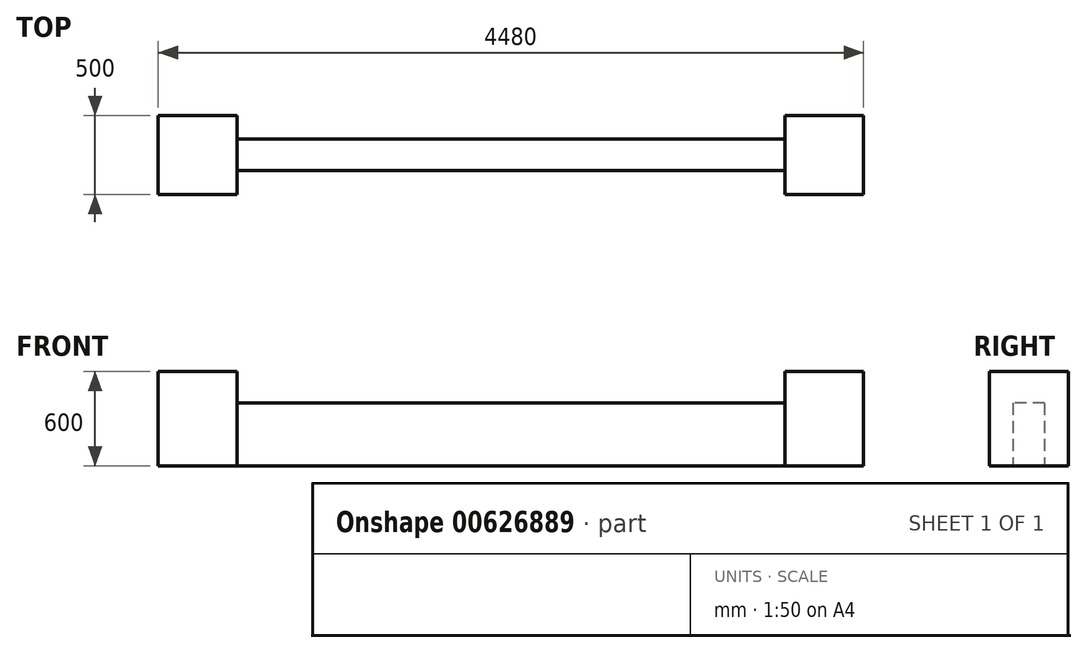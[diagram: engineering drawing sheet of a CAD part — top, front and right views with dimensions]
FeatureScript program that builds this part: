
annotation { "Feature Type Name" : "Feature", "Feature Type Description" : "" }
export const myFeature = defineFeature(function(context is Context, id is Id, definition is map)
    precondition{}
    {
        {
            var Q0;
            Q0=qCreatedBy(makeId("Top.planeOp"),FACE);
            var sketch = newSketch(context, id + "F0", { "sketchPlane" : qUnion([Q0])});
            skLineSegment(sketch, "E0", {"start": v(-1541.48, -106.4) * mm, "end": v(-1541.48, -606.4) * mm});
            skLineSegment(sketch, "E1", {"start": v(-1541.48, -606.4) * mm, "end": v(-1041.48, -606.4) * mm});
            skLineSegment(sketch, "E2", {"start": v(-1041.48, -606.4) * mm, "end": v(-1041.48, -456.4) * mm});
            skLineSegment(sketch, "E3", {"start": v(-1041.48, -456.4) * mm, "end": v(2438.52, -456.4) * mm});
            skLineSegment(sketch, "E4", {"start": v(2438.52, -456.4) * mm, "end": v(2438.52, -606.4) * mm});
            skLineSegment(sketch, "E5", {"start": v(2438.52, -606.4) * mm, "end": v(2938.52, -606.4) * mm});
            skLineSegment(sketch, "E6", {"start": v(2938.52, -606.4) * mm, "end": v(2938.52, -106.4) * mm});
            skLineSegment(sketch, "E7", {"start": v(2938.52, -106.4) * mm, "end": v(2438.52, -106.4) * mm});
            skLineSegment(sketch, "E8", {"start": v(2438.52, -106.4) * mm, "end": v(2438.52, -256.4) * mm});
            skLineSegment(sketch, "E9", {"start": v(2438.52, -256.4) * mm, "end": v(-1041.48, -256.4) * mm});
            skLineSegment(sketch, "E10", {"start": v(-1041.48, -256.4) * mm, "end": v(-1041.48, -106.4) * mm});
            skLineSegment(sketch, "E11", {"start": v(-1541.48, -106.4) * mm, "end": v(-1041.48, -106.4) * mm});
            skLineSegment(sketch, "E12", {"start": v(-1081.48, 332.04) * mm, "end": v(-1081.48, -1348.1) * mm, "construction": true});
            skLineSegment(sketch, "E13", {"start": v(2478.52, 358.87) * mm, "end": v(2478.52, -1348.1) * mm, "construction": true});
            skLineSegment(sketch, "E14", {"start": v(698.52, 382.34) * mm, "end": v(698.52, -1673.4) * mm, "construction": true});
            skSolve(sketch);
        }
        {
            var Q0;
            Q0 = qSketchRegion(id + "F0", true);
            extrude(context, id + "F1", {"entities" : qUnion([Q0]), "depth" : 400 * mm, "offsetDistance" : 25 * mm});
        }
        {
            var Q0;
            Q0=makeQuery(id+"F1.opExtrude","CAP_FACE",FACE,{"disambiguationData":[OSD([sQuery(id+"F0.wireOp",EDGE,"E0"),sQuery(id+"F0.wireOp",EDGE,"E1"),sQuery(id+"F0.wireOp",EDGE,"E2"),sQuery(id+"F0.wireOp",EDGE,"E3"),sQuery(id+"F0.wireOp",EDGE,"E4"),sQuery(id+"F0.wireOp",EDGE,"E5"),sQuery(id+"F0.wireOp",EDGE,"E6"),sQuery(id+"F0.wireOp",EDGE,"E7"),sQuery(id+"F0.wireOp",EDGE,"E8"),sQuery(id+"F0.wireOp",EDGE,"E9"),sQuery(id+"F0.wireOp",EDGE,"E10"),sQuery(id+"F0.wireOp",EDGE,"E11")])],"isStart":false});
            var sketch = newSketch(context, id + "F2", { "sketchPlane" : qUnion([Q0])});
            skLineSegment(sketch, "E15.bottom", {"start": v(-1541.48, -106.4) * mm, "end": v(-1041.48, -106.4) * mm});
            skLineSegment(sketch, "E15.top", {"start": v(-1541.48, -606.4) * mm, "end": v(-1041.48, -606.4) * mm});
            skLineSegment(sketch, "E15.left", {"start": v(-1541.48, -106.4) * mm, "end": v(-1541.48, -606.4) * mm});
            skLineSegment(sketch, "E15.right", {"start": v(-1041.48, -106.4) * mm, "end": v(-1041.48, -606.4) * mm});
            skLineSegment(sketch, "E16.bottom", {"start": v(2438.52, -106.4) * mm, "end": v(2938.52, -106.4) * mm});
            skLineSegment(sketch, "E16.top", {"start": v(2438.52, -606.4) * mm, "end": v(2938.52, -606.4) * mm});
            skLineSegment(sketch, "E16.left", {"start": v(2438.52, -106.4) * mm, "end": v(2438.52, -606.4) * mm});
            skLineSegment(sketch, "E16.right", {"start": v(2938.52, -106.4) * mm, "end": v(2938.52, -606.4) * mm});
            skSolve(sketch);
        }
        {
            var Q0;
            Q0 = qSketchRegion(id + "F2", true);
            extrude(context, id + "F3", {"entities" : qUnion([Q0]), "operationType" : NewBodyOperationType.ADD, "depth" : 200 * mm, "offsetDistance" : 25 * mm});
        }
    });
